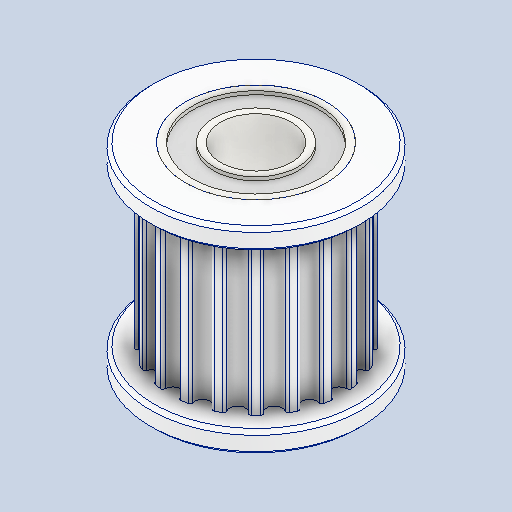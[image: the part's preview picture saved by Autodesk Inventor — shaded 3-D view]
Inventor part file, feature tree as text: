
AUTODESK INVENTOR PART (.ipt)
format: ipt  version: 2024 (Build 280153000, 153)  size: 507,904 bytes
history: native  units: mm
features: extrude x3, other x3, plane x2, revolve x1, chamfer x1, pattern_circular x1, sketch x1, mirror x1, projected_geometry x1
ambient origin geometry x8: Origin, YZ Plane, XZ Plane, XY Plane, X Axis, Y Axis, Z Axis, Center Point
bodies: Solid1 (feature_tree)
feature tree (14):
  revolve  "Revolution1"  [1 undecoded]
  chamfer  "Chamfer2"  Distance=14.0mm
  extrude  "Extrusion2"  Depth=11.0mm
  pattern_circular  "Circular Pattern1"  [2 undecoded]
  plane  "Work Plane5"
  sketch  "Sketch6"  dims[d0=7.5mm d1=5.0mm d2=14.0mm d3=11.0mm d4=1.5mm d5=6.11mm d6=90.0deg d22=12.22mm d23=0.15mm d24=0.555mm d25=0.75mm d26=0.1mm d27=0.0mm d28=200.0mm d29=360.0deg d31=0.25mm d32=2.0mm d33=45.0deg d35=-2.0mm d36=10.0mm d37=5.0mm d38=0.5mm d39=0.5mm d40=4.0mm d41=0.0mm d42=3.5mm d43=0.0mm]
  extrude  "Extrusion3"  Depth=6.11mm
  extrude  "Extrusion4"  TaperAngle=90.0deg  [1 undecoded]
  plane  "Work Plane4"
  mirror  "Mirror3"
  other  "Top Bearing"
  other  "Pattern of Top Bearing:1"
  other  "Bottom Bearing"
  projected_geometry  "Project Cut Edges2"
note: 4 required parameter values undecoded (feature->parameter linkage not recoverable at this tier; creation-order binding heuristic only, values carry confidence <= 0.55)